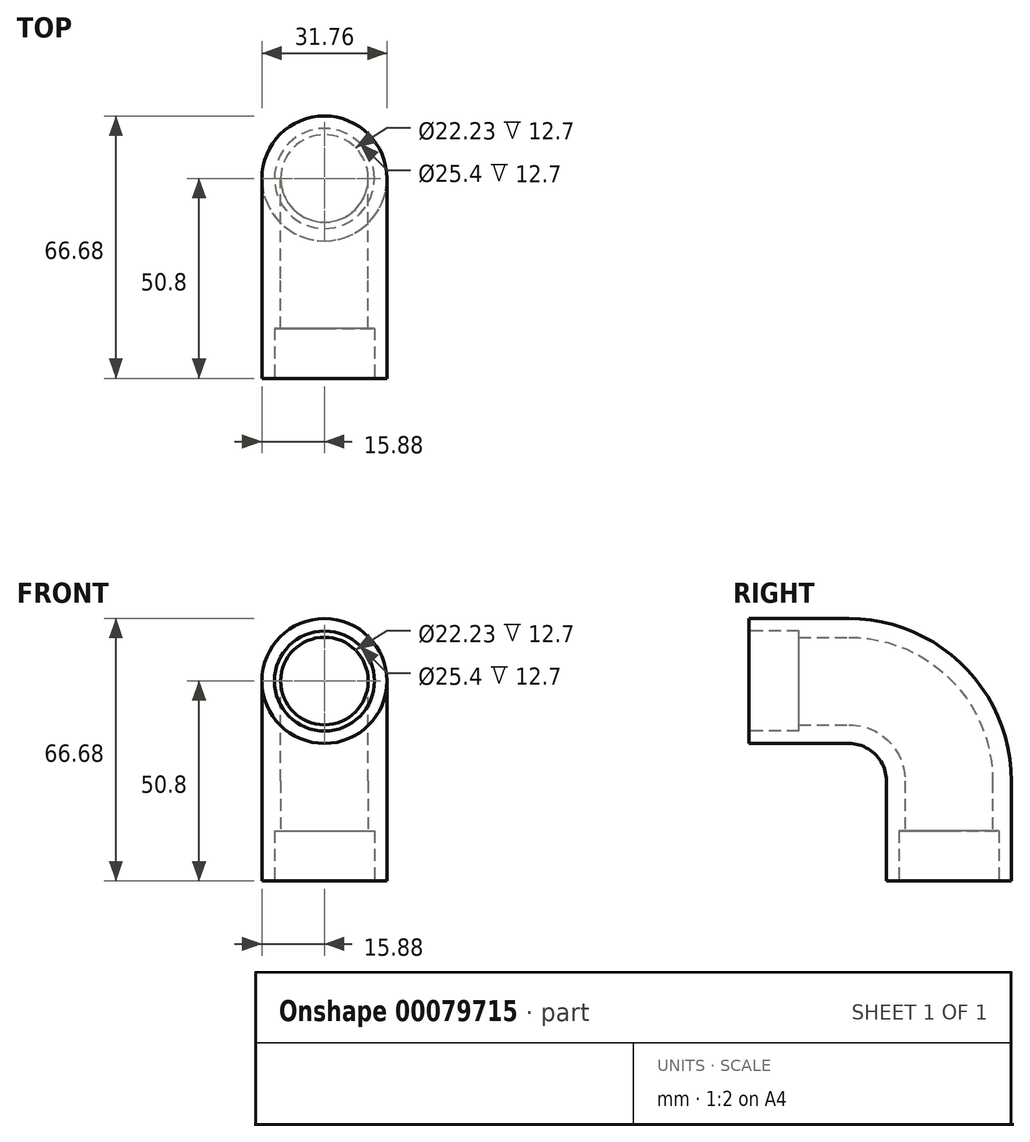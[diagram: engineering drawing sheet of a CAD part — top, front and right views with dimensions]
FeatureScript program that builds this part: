
annotation { "Feature Type Name" : "Feature", "Feature Type Description" : "" }
export const myFeature = defineFeature(function(context is Context, id is Id, definition is map)
    precondition{}
    {
        {
            var Q0;
            Q0=qCreatedBy(makeId("Front.planeOp"),FACE);
            var sketch = newSketch(context, id + "F0", { "sketchPlane" : qUnion([Q0])});
            skCircle(sketch, "E0", {"center": v(0, 0) * mm, "radius": 15.88 * mm});
            skCircle(sketch, "E1", {"center": v(0, 0) * mm, "radius": 11.11 * mm});
            skSolve(sketch);
        }
        {
            var Q0;
            Q0=qCreatedBy(makeId("Right.planeOp"),FACE);
            var sketch = newSketch(context, id + "F1", { "sketchPlane" : qUnion([Q0])});
            skLineSegment(sketch, "E2", {"start": v(0, 0) * mm, "end": v(25.4, 0) * mm});
            skLineSegment(sketch, "E3", {"start": v(50.8, -25.4) * mm, "end": v(50.8, -50.8) * mm});
            skPoint(sketch, "E4.visualSharp", {"position": v(50.8, 0) * mm});
            skArc(sketch, "E4.filletArc", {"start": v(50.8, -25.4) * mm, "mid": v(43.36, -7.44) * mm, "end": v(25.4, 0) * mm});
            skSolve(sketch);
        }
        {
            var Q0;
            Q0=makeQuery(id+"F0.imprint","IMPRINT",FACE,{"disambiguationData":[TD([[makeQuery(id+"F0.imprint","IMPRINT",EDGE,{"derivedFrom":sQuery(id+"F0.wireOp",EDGE,"E0")}),1.0]])]});
            var Q1;
            Q1=sQuery(id+"F1.wireOp",EDGE,"E2");
            var Q2;
            Q2=sQuery(id+"F1.wireOp",EDGE,"E4.filletArc");
            var Q3;
            Q3=sQuery(id+"F1.wireOp",EDGE,"E3");
            sweep(context, id + "F2", {"profiles" : qUnion([Q0]), "path" : qUnion([Q1, Q2, Q3])});
        }
        {
            var Q0;
            Q0=makeQuery(id+"F2.opSweep","CAP_FACE",FACE,{"disambiguationData":[OSD([sQuery(id+"F0.wireOp",EDGE,"E0"),sQuery(id+"F0.wireOp",EDGE,"E1"),sQuery(id+"F1.wireOp",VERTEX,"E2.start")])],"isStart":true});
            var sketch = newSketch(context, id + "F3", { "sketchPlane" : qUnion([Q0])});
            skCircle(sketch, "E5", {"center": v(0, 0) * mm, "radius": 12.7 * mm});
            skSolve(sketch);
        }
        {
            var Q0;
            Q0 = qSketchRegion(id + "F3", true);
            extrude(context, id + "F4", {"entities" : qUnion([Q0]), "operationType" : NewBodyOperationType.REMOVE, "oppositeDirection" : true, "depth" : 12.7 * mm});
        }
        {
            var Q0;
            Q0=makeQuery(id+"F2.opSweep","CAP_FACE",FACE,{"disambiguationData":[OSD([sQuery(id+"F0.wireOp",EDGE,"E0"),sQuery(id+"F0.wireOp",EDGE,"E1"),sQuery(id+"F1.wireOp",VERTEX,"E3.end")])],"isStart":false});
            var sketch = newSketch(context, id + "F5", { "sketchPlane" : qUnion([Q0])});
            skCircle(sketch, "E6", {"center": v(0, -50.8) * mm, "radius": 12.7 * mm});
            skSolve(sketch);
        }
        {
            var Q0;
            Q0 = qSketchRegion(id + "F5", true);
            extrude(context, id + "F6", {"entities" : qUnion([Q0]), "operationType" : NewBodyOperationType.REMOVE, "oppositeDirection" : true, "depth" : 12.7 * mm});
        }
    });
